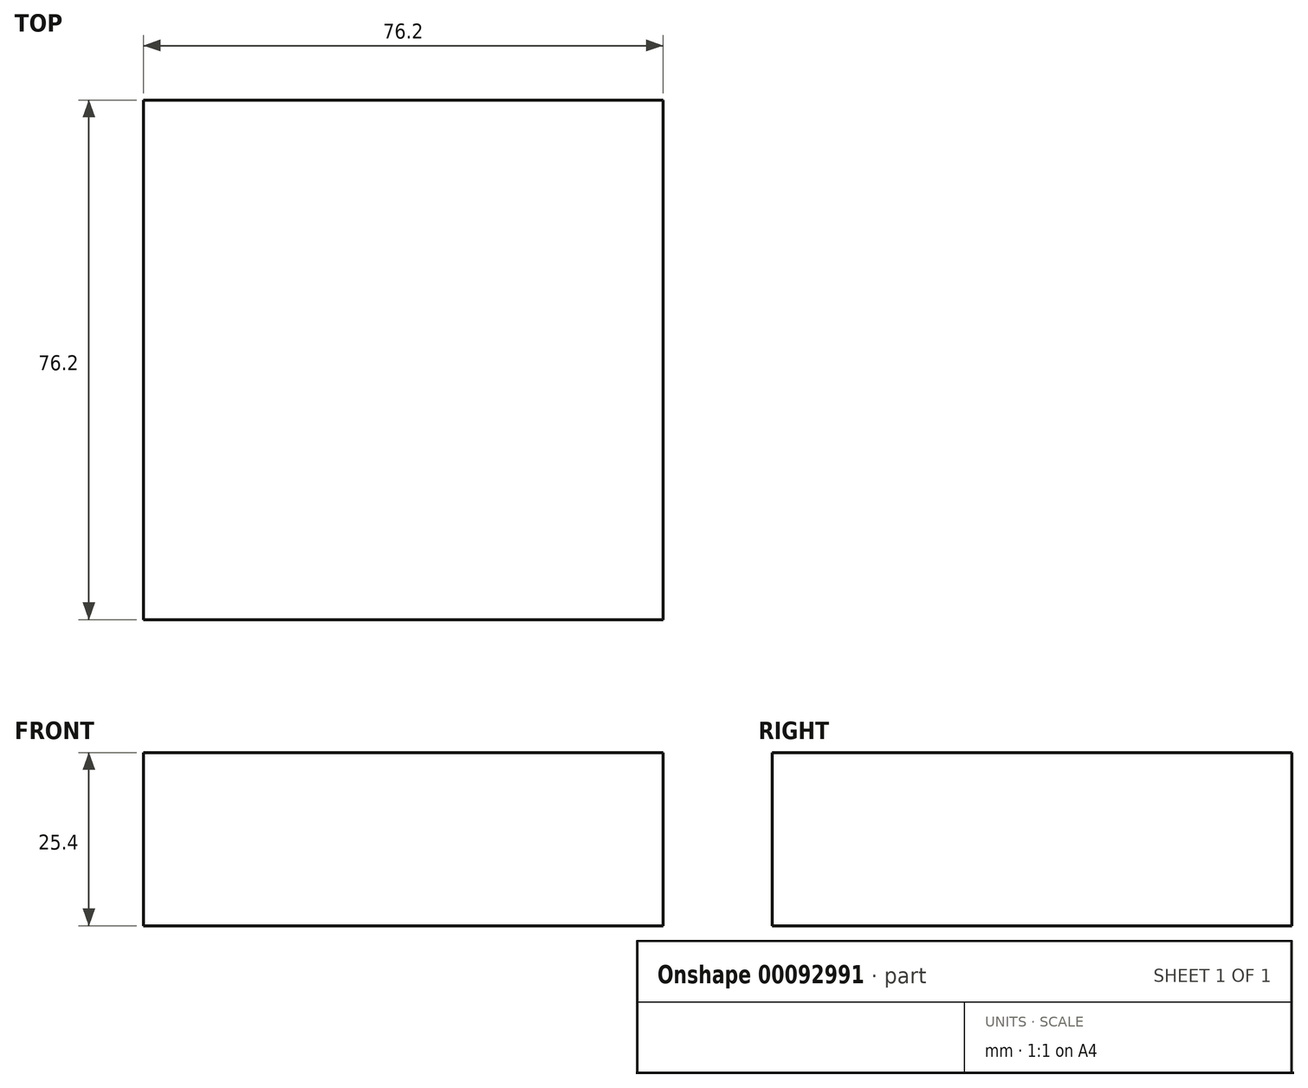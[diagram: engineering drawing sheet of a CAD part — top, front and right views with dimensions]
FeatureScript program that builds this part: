
annotation { "Feature Type Name" : "Feature", "Feature Type Description" : "" }
export const myFeature = defineFeature(function(context is Context, id is Id, definition is map)
    precondition{}
    {
        {
            var Q0;
            Q0=qCreatedBy(makeId("Top.planeOp"),FACE);
            var sketch = newSketch(context, id + "F0", { "sketchPlane" : qUnion([Q0])});
            skLineSegment(sketch, "E0.bottom", {"start": v(38.1, -38.1) * mm, "end": v(-38.1, -38.1) * mm});
            skLineSegment(sketch, "E0.top", {"start": v(38.1, 38.1) * mm, "end": v(-38.1, 38.1) * mm});
            skLineSegment(sketch, "E0.left", {"start": v(38.1, -38.1) * mm, "end": v(38.1, 38.1) * mm});
            skLineSegment(sketch, "E0.right", {"start": v(-38.1, -38.1) * mm, "end": v(-38.1, 38.1) * mm});
            skPoint(sketch, "E0.middle", {"position": v(0, 0) * mm});
            skSolve(sketch);
        }
        {
            var Q0;
            Q0=makeQuery(id+"F0.imprint","IMPRINT",FACE,{"disambiguationData":[TD([[makeQuery(id+"F0.imprint","IMPRINT",EDGE,{"derivedFrom":sQuery(id+"F0.wireOp",EDGE,"E0.bottom")}),-1.0]])]});
            extrude(context, id + "F1", {"entities" : qUnion([Q0]), "depth" : 25.4 * mm});
        }
    });
